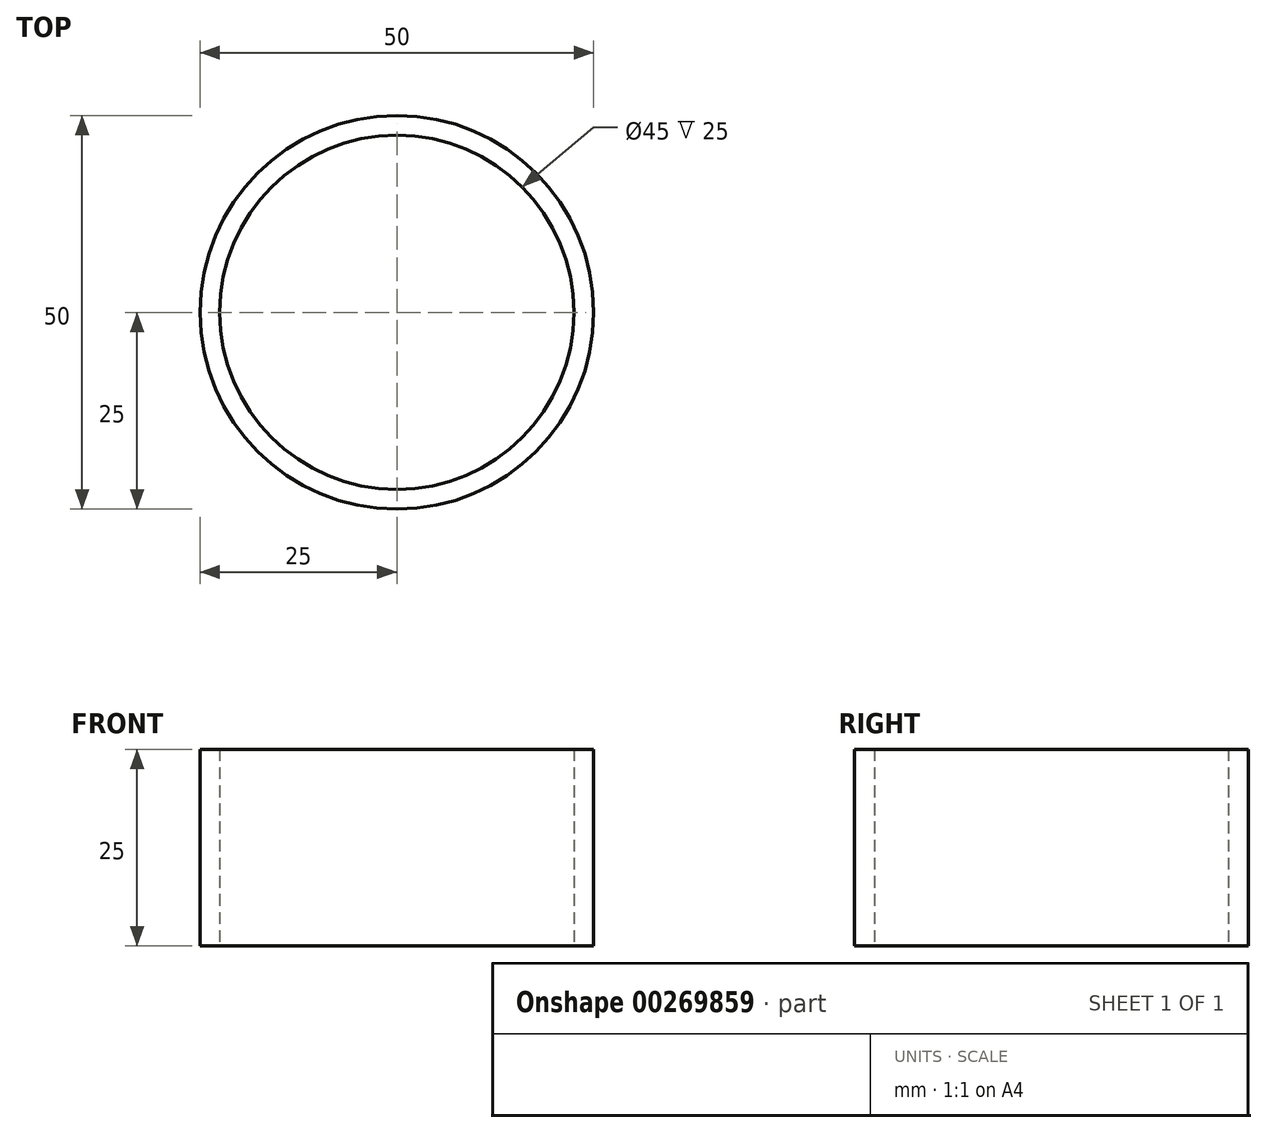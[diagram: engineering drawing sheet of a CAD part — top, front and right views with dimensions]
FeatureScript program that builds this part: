
annotation { "Feature Type Name" : "Feature", "Feature Type Description" : "" }
export const myFeature = defineFeature(function(context is Context, id is Id, definition is map)
    precondition{}
    {
        {
            var Q0;
            Q0=qCreatedBy(makeId("Top.planeOp"),FACE);
            var sketch = newSketch(context, id + "F0", { "sketchPlane" : qUnion([Q0])});
            skCircle(sketch, "E0", {"center": v(0, 0) * mm, "radius": 25 * mm});
            skSolve(sketch);
        }
        {
            var Q0;
            Q0=makeQuery(id+"F0.imprint","IMPRINT",FACE,{"disambiguationData":[TD([[makeQuery(id+"F0.imprint","IMPRINT",EDGE,{"derivedFrom":sQuery(id+"F0.wireOp",EDGE,"E0")}),1.0]])]});
            extrude(context, id + "F1", {"entities" : qUnion([Q0]), "depth" : 25 * mm});
        }
        {
            var Q0;
            Q0=makeQuery(id+"F1.opExtrude","CAP_FACE",FACE,{"disambiguationData":[OSD([sQuery(id+"F0.wireOp",EDGE,"E0")])],"isStart":false});
            var Q1;
            Q1=makeQuery(id+"F1.opExtrude","SWEPT_BODY",BODY,{"disambiguationData":[OSD([sQuery(id+"F0.wireOp",EDGE,"E0")])]});
            shell(context, id + "F2", {"entities" : qUnion([Q0]), "parts" : qUnion([Q1]), "thickness" : 2.5 * mm});
        }
        {
            var Q0;
            {var subQ0=sQuery(id+"F0.wireOp",EDGE,"E0");Q0=makeQuery(id+"F2.opShell","OFFSET_FACE",FACE,{"disambiguationData":[OSD([subQ0]),TDD([makeQuery(id+"F1.opExtrude","CAP_FACE",FACE,{"disambiguationData":[OSD([subQ0])],"isStart":true})])]});}
            var sketch = newSketch(context, id + "F3", { "sketchPlane" : qUnion([Q0])});
            skSolve(sketch);
        }
        {
            var Q0;
            {var subQ0=sQuery(id+"F0.wireOp",EDGE,"E0");Q0=makeQuery(id+"F3.imprint","IMPRINT",FACE,{"disambiguationData":[TD([[makeQuery(id+"F3.imprint","IMPRINT",EDGE,{"derivedFrom":makeQuery(id+"F2.opShell","OFFSET_EDGE",EDGE,{"disambiguationData":[OSD([subQ0]),TDD([makeQuery(id+"F1.opExtrude","CAP_EDGE",EDGE,{"disambiguationData":[OSD([subQ0])],"isStart":true})])]})}),1.0]])]});}
            extrude(context, id + "F4", {"entities" : qUnion([Q0]), "operationType" : NewBodyOperationType.REMOVE, "oppositeDirection" : true, "depth" : 2.5 * mm});
        }
    });
